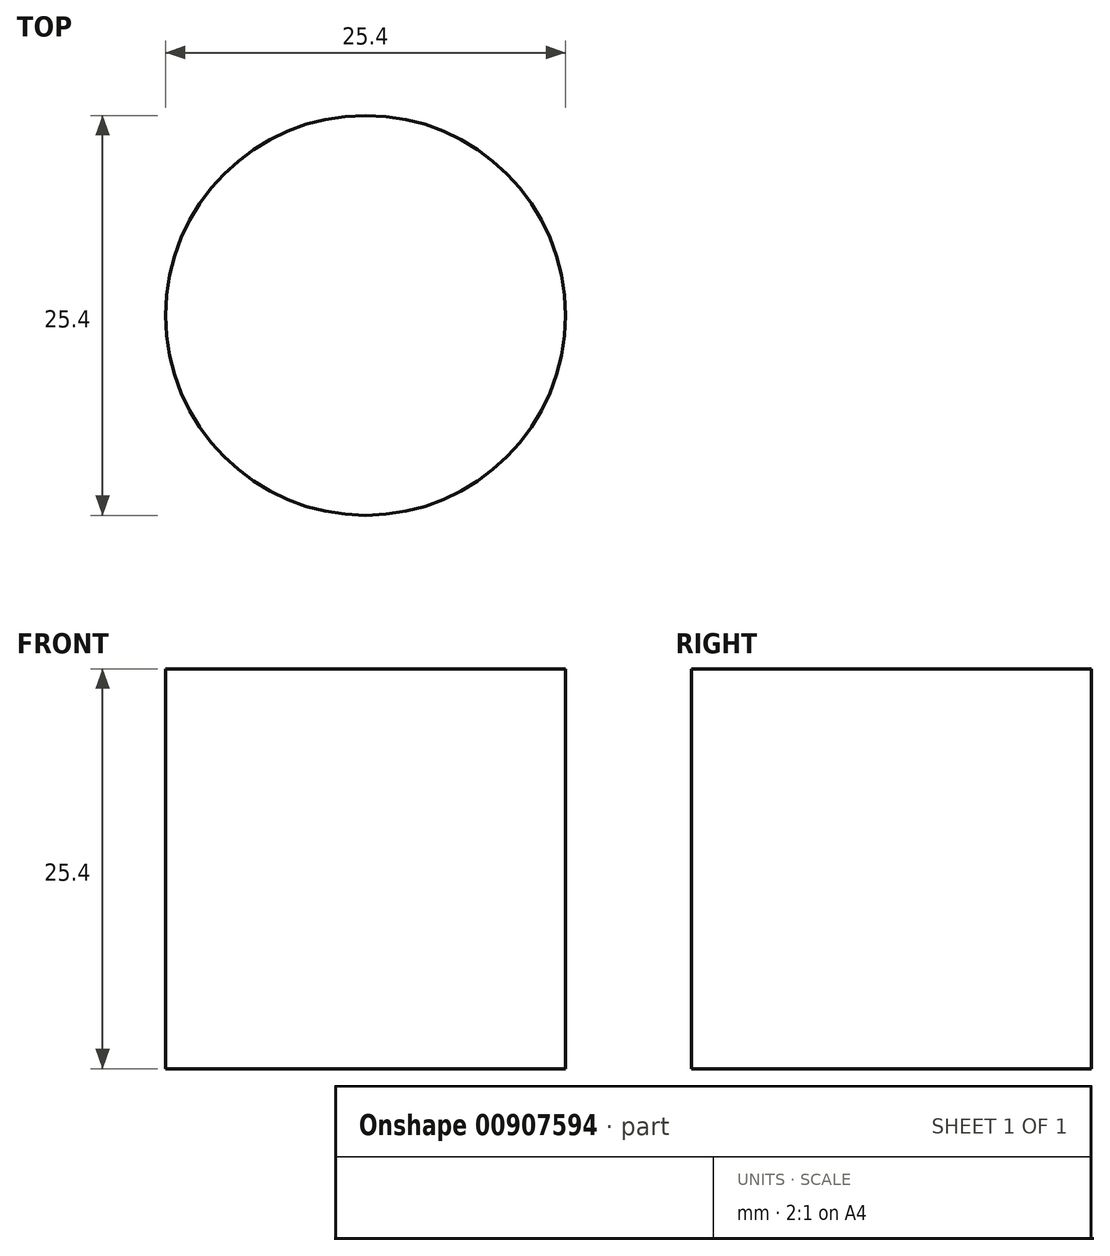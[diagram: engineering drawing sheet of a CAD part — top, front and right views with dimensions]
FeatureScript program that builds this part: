
annotation { "Feature Type Name" : "Feature", "Feature Type Description" : "" }
export const myFeature = defineFeature(function(context is Context, id is Id, definition is map)
    precondition{}
    {
        {
            var Q0;
            Q0=qCreatedBy(makeId("Top.planeOp"),FACE);
            var sketch = newSketch(context, id + "F0", { "sketchPlane" : qUnion([Q0])});
            skCircle(sketch, "E0", {"center": v(0, 0) * mm, "radius": 12.7 * mm});
            skSolve(sketch);
        }
        {
            var Q0;
            Q0 = qSketchRegion(id + "F0", true);
            extrude(context, id + "F1", {"entities" : qUnion([Q0]), "depth" : 25.4 * mm, "offsetDistance" : 25.4 * mm});
        }
    });
